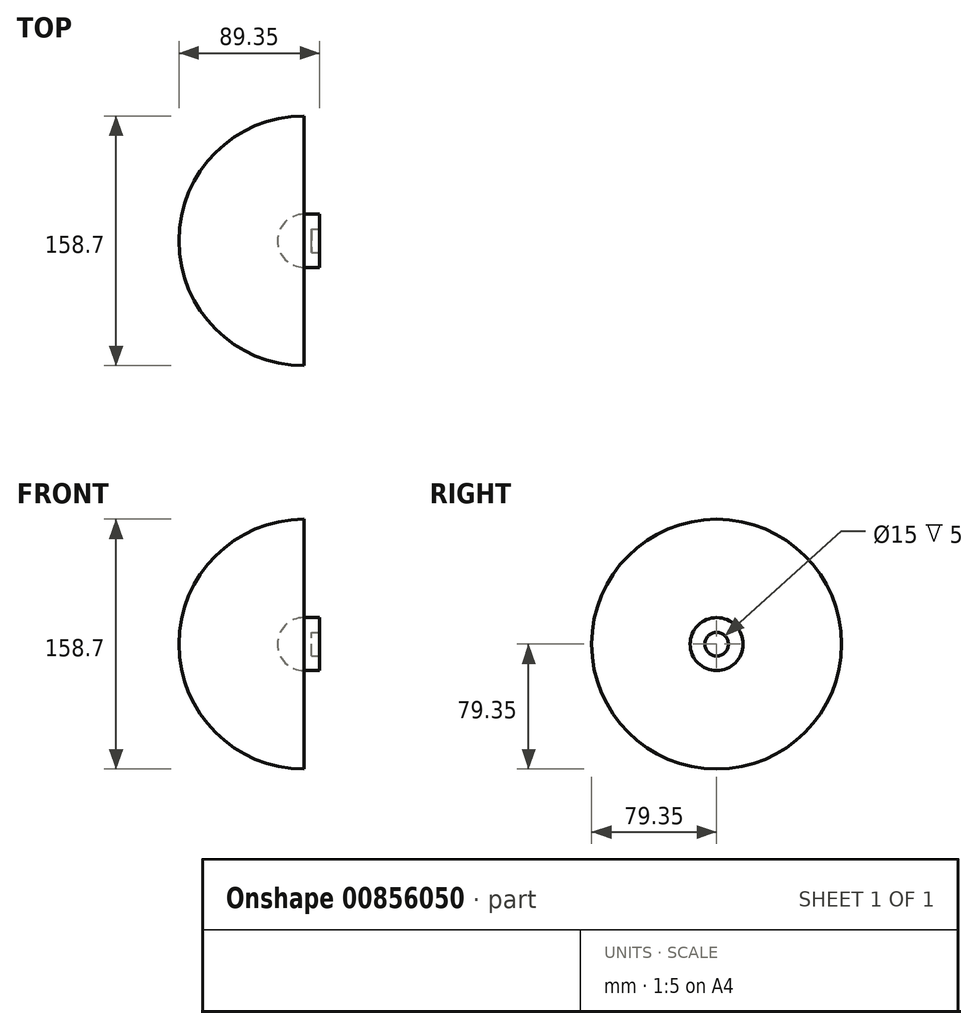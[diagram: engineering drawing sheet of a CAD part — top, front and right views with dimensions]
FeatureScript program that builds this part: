
annotation { "Feature Type Name" : "Feature", "Feature Type Description" : "" }
export const myFeature = defineFeature(function(context is Context, id is Id, definition is map)
    precondition{}
    {
        {
            var Q0;
            Q0=qCreatedBy(makeId("Right.planeOp"),FACE);
            var sketch = newSketch(context, id + "F0", { "sketchPlane" : qUnion([Q0])});
            skCircle(sketch, "E0", {"center": v(0, 0) * mm, "radius": 16.85 * mm});
            skSolve(sketch);
        }
        {
            var Q0;
            Q0=makeQuery(id+"F0.imprint","IMPRINT",FACE,{"disambiguationData":[TD([[makeQuery(id+"F0.imprint","IMPRINT",EDGE,{"derivedFrom":sQuery(id+"F0.wireOp",EDGE,"E0")}),1.0]])]});
            extrude(context, id + "F1", {"entities" : qUnion([Q0]), "depth" : 10 * mm, "offsetDistance" : 25 * mm});
        }
        {
            var Q0;
            Q0=makeQuery(id+"F1.opExtrude","CAP_FACE",FACE,{"disambiguationData":[OSD([sQuery(id+"F0.wireOp",EDGE,"E0")])],"isStart":false});
            var sketch = newSketch(context, id + "F2", { "sketchPlane" : qUnion([Q0])});
            skCircle(sketch, "E1", {"center": v(0, 0) * mm, "radius": 7.5 * mm});
            skSolve(sketch);
        }
        {
            var Q0;
            Q0=makeQuery(id+"F2.imprint","IMPRINT",FACE,{"disambiguationData":[TD([[makeQuery(id+"F2.imprint","IMPRINT",EDGE,{"derivedFrom":sQuery(id+"F2.wireOp",EDGE,"E1")}),1.0]])]});
            extrude(context, id + "F3", {"entities" : qUnion([Q0]), "operationType" : NewBodyOperationType.REMOVE, "oppositeDirection" : true, "depth" : 5 * mm, "offsetDistance" : 25 * mm});
        }
        {
            var Q0;
            Q0=makeQuery(id+"F1.opExtrude","CAP_FACE",FACE,{"disambiguationData":[OSD([sQuery(id+"F0.wireOp",EDGE,"E0")])],"isStart":true});
            var sketch = newSketch(context, id + "F4", { "sketchPlane" : qUnion([Q0])});
            skArc(sketch, "E2", {"start": v(79.35, 0) * mm, "mid": v(0, 79.35) * mm, "end": v(-79.35, 0) * mm});
            skLineSegment(sketch, "E3", {"start": v(-79.35, 0) * mm, "end": v(79.35, 0) * mm});
            skSolve(sketch);
        }
        {
            var Q0;
            {var subQ0=sQuery(id+"F4.wireOp",EDGE,"E2");Q0=makeQuery(id+"F4.imprint","IMPRINT",FACE,{"disambiguationData":[TD([[makeQuery(id+"F4.imprint","IMPRINT",EDGE,{"derivedFrom":subQ0}),1.0]])]});}
            var Q1;
            Q1=sQuery(id+"F4.wireOp",EDGE,"E3");
            revolve(context, id + "F5", {"surfaceOperationType" : NewSurfaceOperationType.NEW, "entities" : qUnion([Q0]), "axis" : qUnion([Q1]), "revolveType" : RevolveType.TWO_DIRECTIONS, "angle" : 180 * degree, "angleBack" : 360 * degree});
        }
    });
